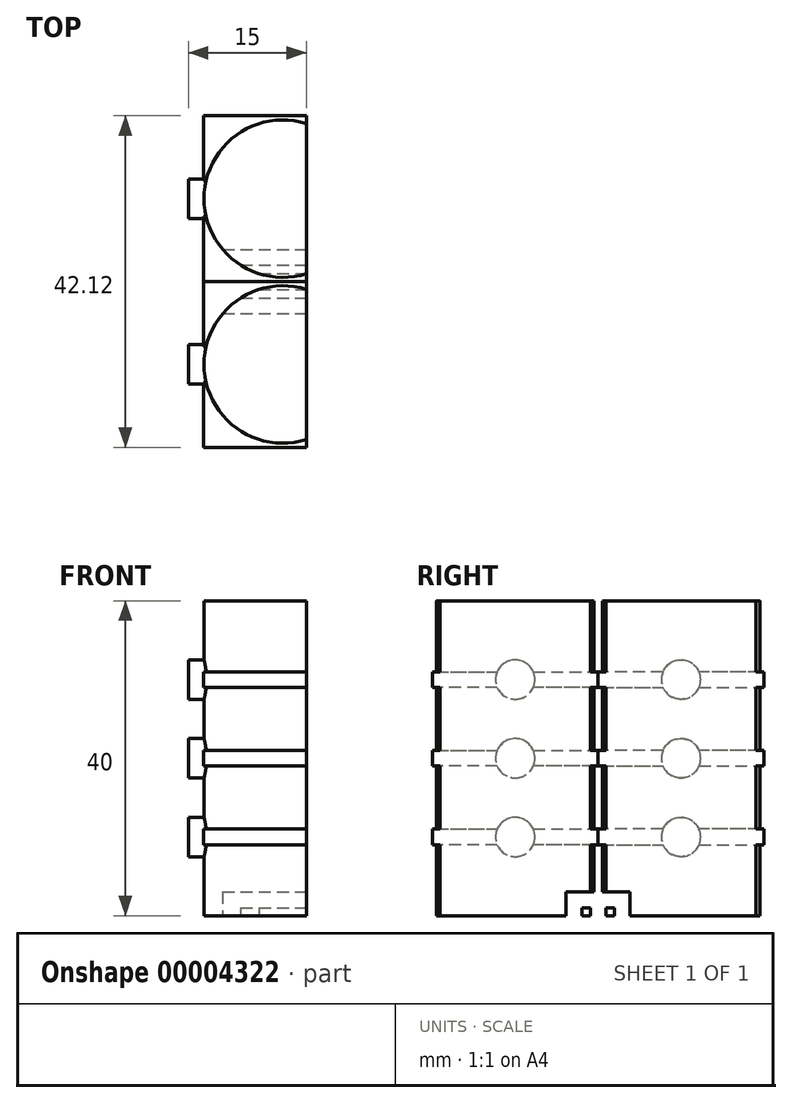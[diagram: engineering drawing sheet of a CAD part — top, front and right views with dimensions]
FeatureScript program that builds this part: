
annotation { "Feature Type Name" : "Feature", "Feature Type Description" : "" }
export const myFeature = defineFeature(function(context is Context, id is Id, definition is map)
    precondition{}
    {
        {
            var Q0;
            Q0=qCreatedBy(makeId("Top.planeOp"),FACE);
            var sketch = newSketch(context, id + "F0", { "sketchPlane" : qUnion([Q0])});
            skArc(sketch, "E0", {"start": v(3, 9.54) * mm, "mid": v(-10, 0) * mm, "end": v(3, -9.54) * mm});
            skLineSegment(sketch, "E1.0", {"start": v(3, -9.54) * mm, "end": v(3, 9.54) * mm});
            skLineSegment(sketch, "E2", {"start": v(3, 0) * mm, "end": v(-10, 0) * mm});
            skSolve(sketch);
        }
        {
            var Q0;
            Q0=makeQuery(id+"F0.imprint","IMPRINT",FACE,{"disambiguationData":[TD([[makeQuery(id+"F0.imprint","IMPRINT",EDGE,{"derivedFrom":sQuery(id+"F0.wireOp",EDGE,"E0")}),1.0]])]});
            extrude(context, id + "F1", {"entities" : qUnion([Q0]), "depth" : 40 * mm});
        }
        {
            var Q0;
            Q0=makeQuery(id+"F1.opExtrude","SWEPT_FACE",FACE,{"disambiguationData":[OSD([sQuery(id+"F0.wireOp",EDGE,"E1.0")])]});
            var sketch = newSketch(context, id + "F2", { "sketchPlane" : qUnion([Q0])});
            skLineSegment(sketch, "E3.0", {"start": v(-9.53, 1) * mm, "end": v(12.26, 1) * mm});
            skLineSegment(sketch, "E4.0", {"start": v(-9.53, 3) * mm, "end": v(12.26, 3) * mm});
            skLineSegment(sketch, "E5", {"start": v(12.26, 3) * mm, "end": v(12.26, 1) * mm});
            skLineSegment(sketch, "E6", {"start": v(9.54, 1) * mm, "end": v(9.54, 3) * mm});
            skLineSegment(sketch, "E7.0", {"start": v(6.46, 1) * mm, "end": v(6.46, 3) * mm});
            skLineSegment(sketch, "E8", {"start": v(9.54, 1) * mm, "end": v(8.46, 1) * mm});
            skLineSegment(sketch, "E9", {"start": v(8.46, 1) * mm, "end": v(8.46, 0) * mm});
            skLineSegment(sketch, "E10", {"start": v(8.46, 0) * mm, "end": v(9.54, 0) * mm});
            skLineSegment(sketch, "E11", {"start": v(9.54, 0) * mm, "end": v(9.54, 1) * mm});
            skLineSegment(sketch, "E12", {"start": v(8.46, 0) * mm, "end": v(6.46, 0) * mm});
            skLineSegment(sketch, "E13", {"start": v(6.46, 0) * mm, "end": v(6.46, 1) * mm});
            skLineSegment(sketch, "E14.0", {"start": v(12.04, 0) * mm, "end": v(12.04, 1) * mm});
            skLineSegment(sketch, "E15", {"start": v(12.04, 0) * mm, "end": v(9.54, 0) * mm});
            skSolve(sketch);
        }
        {
            var Q0;
            {var subQ2=sQuery(id+"F2.wireOp",EDGE,"E6");Q0=makeQuery(id+"F2.imprint","IMPRINT",FACE,{"disambiguationData":[TD([[makeQuery(id+"F2.imprint","IMPRINT",EDGE,{"derivedFrom":subQ2}),-1.0]])]});}
            var Q1;
            {var subQ1=sQuery(id+"F2.wireOp",EDGE,"E9");Q1=makeQuery(id+"F2.imprint","IMPRINT",FACE,{"disambiguationData":[TD([[makeQuery(id+"F2.imprint","IMPRINT",EDGE,{"derivedFrom":subQ1}),-1.0]])]});}
            var Q2;
            {var subQ1=sQuery(id+"F2.wireOp",EDGE,"E5");Q2=makeQuery(id+"F2.imprint","IMPRINT",FACE,{"disambiguationData":[TD([[makeQuery(id+"F2.imprint","IMPRINT",EDGE,{"derivedFrom":subQ1}),-1.0]])]});}
            var Q3;
            Q3=makeQuery(id+"F2.imprint","IMPRINT",FACE,{"disambiguationData":[TD([[makeQuery(id+"F2.imprint","IMPRINT",EDGE,{"derivedFrom":sQuery(id+"F2.wireOp",EDGE,"E8")}),1.0]])]});
            var Q4;
            {var subQ1=sQuery(id+"F2.wireOp",EDGE,"E11");Q4=makeQuery(id+"F2.imprint","IMPRINT",FACE,{"disambiguationData":[TD([[makeQuery(id+"F2.imprint","IMPRINT",EDGE,{"derivedFrom":subQ1}),1.0]])]});}
            extrude(context, id + "F3", {"entities" : qUnion([Q0, Q1, Q2, Q3, Q4]), "operationType" : NewBodyOperationType.REMOVE, "oppositeDirection" : true, "depth" : 15.48 * mm});
        }
        {
            var Q0;
            Q0=qCreatedBy(makeId("Right.planeOp"),FACE);
            var sketch = newSketch(context, id + "F4", { "sketchPlane" : qUnion([Q0])});
            skLineSegment(sketch, "E16", {"start": v(0, 0) * mm, "end": v(0, 40) * mm});
            skLineSegment(sketch, "E17", {"start": v(0, 0) * mm, "end": v(-4.23, 0) * mm});
            skLineSegment(sketch, "E18.0", {"start": v(0, 10) * mm, "end": v(-4.23, 10) * mm});
            skLineSegment(sketch, "E19.0", {"start": v(0, 20) * mm, "end": v(-4.23, 20) * mm});
            skLineSegment(sketch, "E20.0", {"start": v(0, 30) * mm, "end": v(-4.23, 30) * mm});
            skCircle(sketch, "E21", {"center": v(0, 10) * mm, "radius": 2.5 * mm});
            skCircle(sketch, "E22", {"center": v(0, 20) * mm, "radius": 2.5 * mm});
            skCircle(sketch, "E23", {"center": v(0, 30) * mm, "radius": 2.5 * mm});
            skSolve(sketch);
        }
        {
            var Q0;
            {var subQ1=sQuery(id+"F4.wireOp",EDGE,"E16");var subQ4=makeQuery(id+"F4.imprint","INTERSECT",VERTEX,{"derivedFrom":[subQ1,sQuery(id+"F4.wireOp",EDGE,"E20.0")]});Q0=makeQuery(id+"F4.imprint","IMPRINT",FACE,{"disambiguationData":[TD([[makeQuery(id+"F4.imprint","IMPRINT",EDGE,{"disambiguationData":[TD([[subQ4,1.0]])],"derivedFrom":subQ1}),-1.0]])]});}
            var Q1;
            {var subQ1=sQuery(id+"F4.wireOp",EDGE,"E20.0");var subQ3=sQuery(id+"F4.wireOp",EDGE,"E16");var subQ5=makeQuery(id+"F4.imprint","INTERSECT",VERTEX,{"derivedFrom":[subQ3,subQ1]});Q1=makeQuery(id+"F4.imprint","IMPRINT",FACE,{"disambiguationData":[TD([[makeQuery(id+"F4.imprint","IMPRINT",EDGE,{"disambiguationData":[TD([[subQ5,1.0]])],"derivedFrom":subQ3}),1.0]])]});}
            var Q2;
            {var subQ1=sQuery(id+"F4.wireOp",EDGE,"E20.0");var subQ3=sQuery(id+"F4.wireOp",EDGE,"E16");var subQ5=makeQuery(id+"F4.imprint","INTERSECT",VERTEX,{"derivedFrom":[subQ3,subQ1]});Q2=makeQuery(id+"F4.imprint","IMPRINT",FACE,{"disambiguationData":[TD([[makeQuery(id+"F4.imprint","IMPRINT",EDGE,{"disambiguationData":[TD([[subQ5,-1.0]])],"derivedFrom":subQ3}),1.0]])]});}
            var Q3;
            {var subQ1=sQuery(id+"F4.wireOp",EDGE,"E19.0");var subQ3=sQuery(id+"F4.wireOp",EDGE,"E16");var subQ5=makeQuery(id+"F4.imprint","INTERSECT",VERTEX,{"derivedFrom":[subQ3,subQ1]});Q3=makeQuery(id+"F4.imprint","IMPRINT",FACE,{"disambiguationData":[TD([[makeQuery(id+"F4.imprint","IMPRINT",EDGE,{"disambiguationData":[TD([[subQ5,-1.0]])],"derivedFrom":subQ3}),1.0]])]});}
            var Q4;
            {var subQ1=sQuery(id+"F4.wireOp",EDGE,"E16");var subQ4=makeQuery(id+"F4.imprint","INTERSECT",VERTEX,{"derivedFrom":[subQ1,sQuery(id+"F4.wireOp",EDGE,"E19.0")]});Q4=makeQuery(id+"F4.imprint","IMPRINT",FACE,{"disambiguationData":[TD([[makeQuery(id+"F4.imprint","IMPRINT",EDGE,{"disambiguationData":[TD([[subQ4,1.0]])],"derivedFrom":subQ1}),-1.0]])]});}
            var Q5;
            {var subQ1=sQuery(id+"F4.wireOp",EDGE,"E16");var subQ4=makeQuery(id+"F4.imprint","INTERSECT",VERTEX,{"derivedFrom":[subQ1,sQuery(id+"F4.wireOp",EDGE,"E18.0")]});Q5=makeQuery(id+"F4.imprint","IMPRINT",FACE,{"disambiguationData":[TD([[makeQuery(id+"F4.imprint","IMPRINT",EDGE,{"disambiguationData":[TD([[subQ4,1.0]])],"derivedFrom":subQ1}),-1.0]])]});}
            var Q6;
            {var subQ1=sQuery(id+"F4.wireOp",EDGE,"E18.0");var subQ3=sQuery(id+"F4.wireOp",EDGE,"E16");var subQ5=makeQuery(id+"F4.imprint","INTERSECT",VERTEX,{"derivedFrom":[subQ3,subQ1]});Q6=makeQuery(id+"F4.imprint","IMPRINT",FACE,{"disambiguationData":[TD([[makeQuery(id+"F4.imprint","IMPRINT",EDGE,{"disambiguationData":[TD([[subQ5,-1.0]])],"derivedFrom":subQ3}),1.0]])]});}
            var Q7;
            {var subQ1=sQuery(id+"F4.wireOp",EDGE,"E18.0");var subQ3=sQuery(id+"F4.wireOp",EDGE,"E16");var subQ5=makeQuery(id+"F4.imprint","INTERSECT",VERTEX,{"derivedFrom":[subQ3,subQ1]});Q7=makeQuery(id+"F4.imprint","IMPRINT",FACE,{"disambiguationData":[TD([[makeQuery(id+"F4.imprint","IMPRINT",EDGE,{"disambiguationData":[TD([[subQ5,1.0]])],"derivedFrom":subQ3}),1.0]])]});}
            var Q8;
            {var subQ1=sQuery(id+"F4.wireOp",EDGE,"E19.0");var subQ3=sQuery(id+"F4.wireOp",EDGE,"E16");var subQ5=makeQuery(id+"F4.imprint","INTERSECT",VERTEX,{"derivedFrom":[subQ3,subQ1]});Q8=makeQuery(id+"F4.imprint","IMPRINT",FACE,{"disambiguationData":[TD([[makeQuery(id+"F4.imprint","IMPRINT",EDGE,{"disambiguationData":[TD([[subQ5,1.0]])],"derivedFrom":subQ3}),1.0]])]});}
            extrude(context, id + "F5", {"entities" : qUnion([Q0, Q1, Q2, Q3, Q4, Q5, Q6, Q7, Q8]), "operationType" : NewBodyOperationType.ADD, "oppositeDirection" : true, "depth" : 12 * mm});
        }
        {
            var Q0;
            Q0=makeQuery(id+"F1.opExtrude","SWEPT_FACE",FACE,{"disambiguationData":[OSD([sQuery(id+"F0.wireOp",EDGE,"E1.0")])]});
            var sketch = newSketch(context, id + "F6", { "sketchPlane" : qUnion([Q0])});
            skLineSegment(sketch, "E24", {"start": v(-9.54, 40) * mm, "end": v(-10.54, 40) * mm});
            skLineSegment(sketch, "E25", {"start": v(9.54, 40) * mm, "end": v(10.54, 40) * mm});
            skLineSegment(sketch, "E26.0", {"start": v(-9.53, 30) * mm, "end": v(-10.53, 30) * mm});
            skLineSegment(sketch, "E27.0", {"start": v(-9.53, 20) * mm, "end": v(-10.53, 20) * mm});
            skLineSegment(sketch, "E28.0", {"start": v(-9.53, 10) * mm, "end": v(-10.53, 10) * mm});
            skLineSegment(sketch, "E29.0", {"start": v(9.53, 30) * mm, "end": v(10.53, 30) * mm});
            skLineSegment(sketch, "E30.0", {"start": v(9.53, 20) * mm, "end": v(10.53, 20) * mm});
            skLineSegment(sketch, "E31.0", {"start": v(9.53, 10) * mm, "end": v(10.53, 10) * mm});
            skLineSegment(sketch, "E32.0", {"start": v(-9.53, 11) * mm, "end": v(-10.53, 11) * mm});
            skLineSegment(sketch, "E33.0", {"start": v(-9.53, 9) * mm, "end": v(-10.53, 9) * mm});
            skLineSegment(sketch, "E34", {"start": v(-10.53, 11) * mm, "end": v(-10.53, 9) * mm});
            skLineSegment(sketch, "E35.0", {"start": v(9.53, 9) * mm, "end": v(10.53, 9) * mm});
            skLineSegment(sketch, "E36.0", {"start": v(9.53, 11) * mm, "end": v(10.53, 11) * mm});
            skLineSegment(sketch, "E37", {"start": v(10.53, 11) * mm, "end": v(10.53, 9) * mm});
            skLineSegment(sketch, "E38.0", {"start": v(-9.53, 21) * mm, "end": v(-10.53, 21) * mm});
            skLineSegment(sketch, "E39.0", {"start": v(-9.53, 19) * mm, "end": v(-10.53, 19) * mm});
            skLineSegment(sketch, "E40", {"start": v(-10.53, 21) * mm, "end": v(-10.53, 19) * mm});
            skLineSegment(sketch, "E41.0", {"start": v(9.53, 19) * mm, "end": v(10.53, 19) * mm});
            skLineSegment(sketch, "E42.0", {"start": v(9.53, 21) * mm, "end": v(10.53, 21) * mm});
            skLineSegment(sketch, "E43", {"start": v(10.53, 21) * mm, "end": v(10.53, 19) * mm});
            skLineSegment(sketch, "E44.0", {"start": v(-9.53, 31) * mm, "end": v(-10.53, 31) * mm});
            skLineSegment(sketch, "E45.0", {"start": v(-9.53, 29) * mm, "end": v(-10.53, 29) * mm});
            skLineSegment(sketch, "E46.0", {"start": v(9.53, 29) * mm, "end": v(10.53, 29) * mm});
            skLineSegment(sketch, "E47.0", {"start": v(9.53, 31) * mm, "end": v(10.53, 31) * mm});
            skLineSegment(sketch, "E48", {"start": v(-10.53, 31) * mm, "end": v(-10.53, 29) * mm});
            skLineSegment(sketch, "E49", {"start": v(10.53, 31) * mm, "end": v(10.53, 29) * mm});
            skLineSegment(sketch, "E50", {"start": v(-9.53, 31) * mm, "end": v(9.53, 31) * mm});
            skLineSegment(sketch, "E51", {"start": v(-9.53, 29) * mm, "end": v(9.53, 29) * mm});
            skLineSegment(sketch, "E52", {"start": v(-9.53, 21) * mm, "end": v(9.53, 21) * mm});
            skLineSegment(sketch, "E53", {"start": v(9.53, 19) * mm, "end": v(-9.53, 19) * mm});
            skLineSegment(sketch, "E54", {"start": v(-9.53, 11) * mm, "end": v(9.53, 11) * mm});
            skLineSegment(sketch, "E55", {"start": v(-9.53, 9) * mm, "end": v(9.53, 9) * mm});
            skSolve(sketch);
        }
        {
            var Q0;
            {var subQ4=sQuery(id+"F6.wireOp",EDGE,"E26.0");Q0=makeQuery(id+"F6.imprint","IMPRINT",FACE,{"disambiguationData":[TD([[makeQuery(id+"F6.imprint","IMPRINT",EDGE,{"derivedFrom":subQ4}),-1.0]])]});}
            var Q1;
            {var subQ4=sQuery(id+"F6.wireOp",EDGE,"E26.0");Q1=makeQuery(id+"F6.imprint","IMPRINT",FACE,{"disambiguationData":[TD([[makeQuery(id+"F6.imprint","IMPRINT",EDGE,{"derivedFrom":subQ4}),1.0]])]});}
            var Q2;
            {var subQ4=sQuery(id+"F6.wireOp",EDGE,"E29.0");Q2=makeQuery(id+"F6.imprint","IMPRINT",FACE,{"disambiguationData":[TD([[makeQuery(id+"F6.imprint","IMPRINT",EDGE,{"derivedFrom":subQ4}),1.0]])]});}
            var Q3;
            {var subQ4=sQuery(id+"F6.wireOp",EDGE,"E29.0");Q3=makeQuery(id+"F6.imprint","IMPRINT",FACE,{"disambiguationData":[TD([[makeQuery(id+"F6.imprint","IMPRINT",EDGE,{"derivedFrom":subQ4}),-1.0]])]});}
            var Q4;
            {var subQ4=sQuery(id+"F6.wireOp",EDGE,"E30.0");Q4=makeQuery(id+"F6.imprint","IMPRINT",FACE,{"disambiguationData":[TD([[makeQuery(id+"F6.imprint","IMPRINT",EDGE,{"derivedFrom":subQ4}),1.0]])]});}
            var Q5;
            {var subQ4=sQuery(id+"F6.wireOp",EDGE,"E30.0");Q5=makeQuery(id+"F6.imprint","IMPRINT",FACE,{"disambiguationData":[TD([[makeQuery(id+"F6.imprint","IMPRINT",EDGE,{"derivedFrom":subQ4}),-1.0]])]});}
            var Q6;
            {var subQ4=sQuery(id+"F6.wireOp",EDGE,"E27.0");Q6=makeQuery(id+"F6.imprint","IMPRINT",FACE,{"disambiguationData":[TD([[makeQuery(id+"F6.imprint","IMPRINT",EDGE,{"derivedFrom":subQ4}),-1.0]])]});}
            var Q7;
            {var subQ4=sQuery(id+"F6.wireOp",EDGE,"E27.0");Q7=makeQuery(id+"F6.imprint","IMPRINT",FACE,{"disambiguationData":[TD([[makeQuery(id+"F6.imprint","IMPRINT",EDGE,{"derivedFrom":subQ4}),1.0]])]});}
            var Q8;
            {var subQ4=sQuery(id+"F6.wireOp",EDGE,"E28.0");Q8=makeQuery(id+"F6.imprint","IMPRINT",FACE,{"disambiguationData":[TD([[makeQuery(id+"F6.imprint","IMPRINT",EDGE,{"derivedFrom":subQ4}),-1.0]])]});}
            var Q9;
            {var subQ4=sQuery(id+"F6.wireOp",EDGE,"E28.0");Q9=makeQuery(id+"F6.imprint","IMPRINT",FACE,{"disambiguationData":[TD([[makeQuery(id+"F6.imprint","IMPRINT",EDGE,{"derivedFrom":subQ4}),1.0]])]});}
            var Q10;
            {var subQ4=sQuery(id+"F6.wireOp",EDGE,"E31.0");Q10=makeQuery(id+"F6.imprint","IMPRINT",FACE,{"disambiguationData":[TD([[makeQuery(id+"F6.imprint","IMPRINT",EDGE,{"derivedFrom":subQ4}),1.0]])]});}
            var Q11;
            {var subQ4=sQuery(id+"F6.wireOp",EDGE,"E31.0");Q11=makeQuery(id+"F6.imprint","IMPRINT",FACE,{"disambiguationData":[TD([[makeQuery(id+"F6.imprint","IMPRINT",EDGE,{"derivedFrom":subQ4}),-1.0]])]});}
            var Q12;
            {var subQ3=sQuery(id+"F6.wireOp",EDGE,"E50");Q12=makeQuery(id+"F6.imprint","IMPRINT",FACE,{"disambiguationData":[TD([[makeQuery(id+"F6.imprint","IMPRINT",EDGE,{"derivedFrom":subQ3}),-1.0]])]});}
            var Q13;
            {var subQ3=sQuery(id+"F6.wireOp",EDGE,"E52");Q13=makeQuery(id+"F6.imprint","IMPRINT",FACE,{"disambiguationData":[TD([[makeQuery(id+"F6.imprint","IMPRINT",EDGE,{"derivedFrom":subQ3}),-1.0]])]});}
            var Q14;
            {var subQ3=sQuery(id+"F6.wireOp",EDGE,"E54");Q14=makeQuery(id+"F6.imprint","IMPRINT",FACE,{"disambiguationData":[TD([[makeQuery(id+"F6.imprint","IMPRINT",EDGE,{"derivedFrom":subQ3}),-1.0]])]});}
            extrude(context, id + "F7", {"entities" : qUnion([Q0, Q1, Q2, Q3, Q4, Q5, Q6, Q7, Q8, Q9, Q10, Q11, Q12, Q13, Q14]), "operationType" : NewBodyOperationType.ADD, "oppositeDirection" : true, "depth" : 13.03 * mm});
        }
        {
            var Q0;
            Q0=makeQuery(id+"F1.opExtrude","SWEPT_BODY",BODY,{"disambiguationData":[OSD([sQuery(id+"F0.wireOp",EDGE,"E0"),sQuery(id+"F0.wireOp",EDGE,"E1.0")])]});
            var Q1;
            Q1=makeQuery(id+"F7.opExtrude","SWEPT_FACE",FACE,{"disambiguationData":[OSD([sQuery(id+"F6.wireOp",EDGE,"E49")])]});
            mirror(context, id + "F8", {"entities" : qUnion([Q0]), "mirrorPlane" : qUnion([Q1])});
        }
    });
